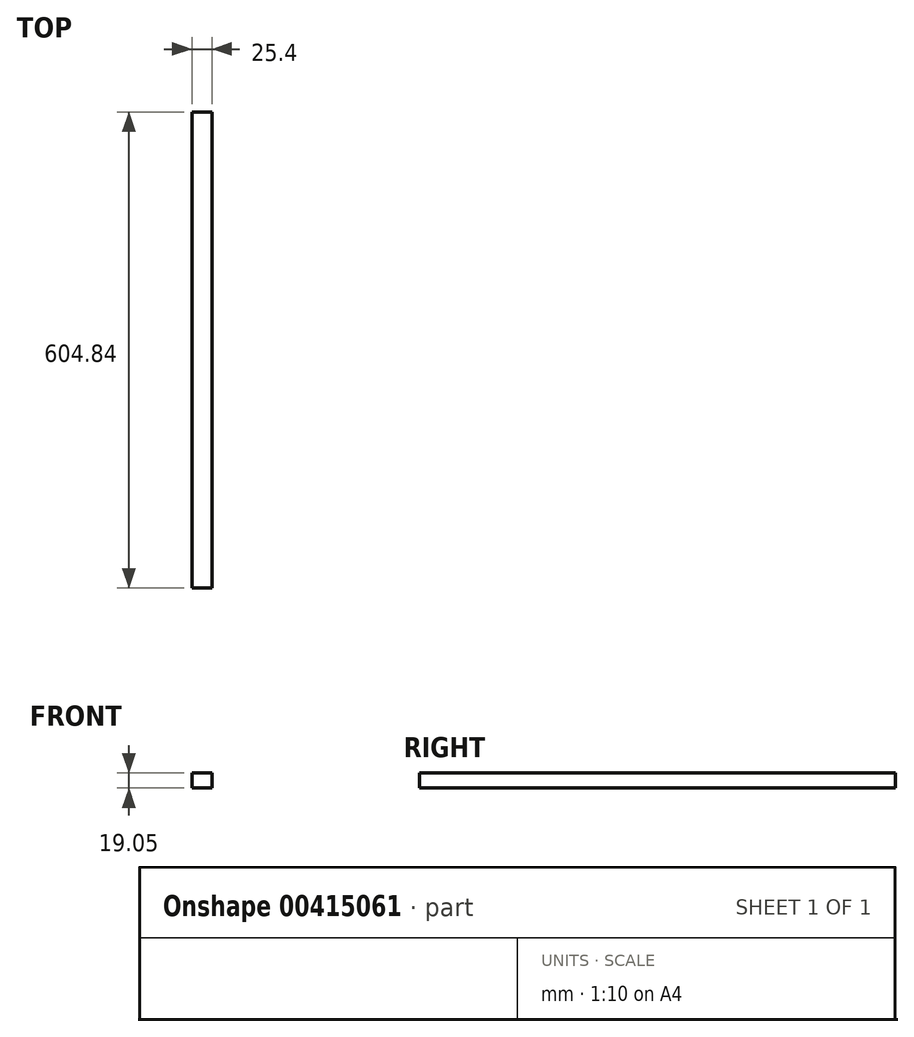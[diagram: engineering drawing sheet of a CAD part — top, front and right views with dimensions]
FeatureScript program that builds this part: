
annotation { "Feature Type Name" : "Feature", "Feature Type Description" : "" }
export const myFeature = defineFeature(function(context is Context, id is Id, definition is map)
    precondition{}
    {
        {
            var Q0;
            Q0=qCreatedBy(makeId("Front.planeOp"),FACE);
            var sketch = newSketch(context, id + "F0", { "sketchPlane" : qUnion([Q0])});
            skLineSegment(sketch, "E0.bottom", {"start": v(0, 0) * mm, "end": v(25.4, 0) * mm});
            skLineSegment(sketch, "E0.top", {"start": v(0, 19.05) * mm, "end": v(25.4, 19.05) * mm});
            skLineSegment(sketch, "E0.left", {"start": v(0, 0) * mm, "end": v(0, 19.05) * mm});
            skLineSegment(sketch, "E0.right", {"start": v(25.4, 0) * mm, "end": v(25.4, 19.05) * mm});
            skSolve(sketch);
        }
        {
            var Q0;
            Q0=makeQuery(id+"F0.imprint","IMPRINT",FACE,{"disambiguationData":[TD([[makeQuery(id+"F0.imprint","IMPRINT",EDGE,{"derivedFrom":sQuery(id+"F0.wireOp",EDGE,"E0.bottom")}),1.0]])]});
            extrude(context, id + "F1", {"entities" : qUnion([Q0]), "depth" : 604.84 * mm, "offsetDistance" : 25.4 * mm});
        }
    });
